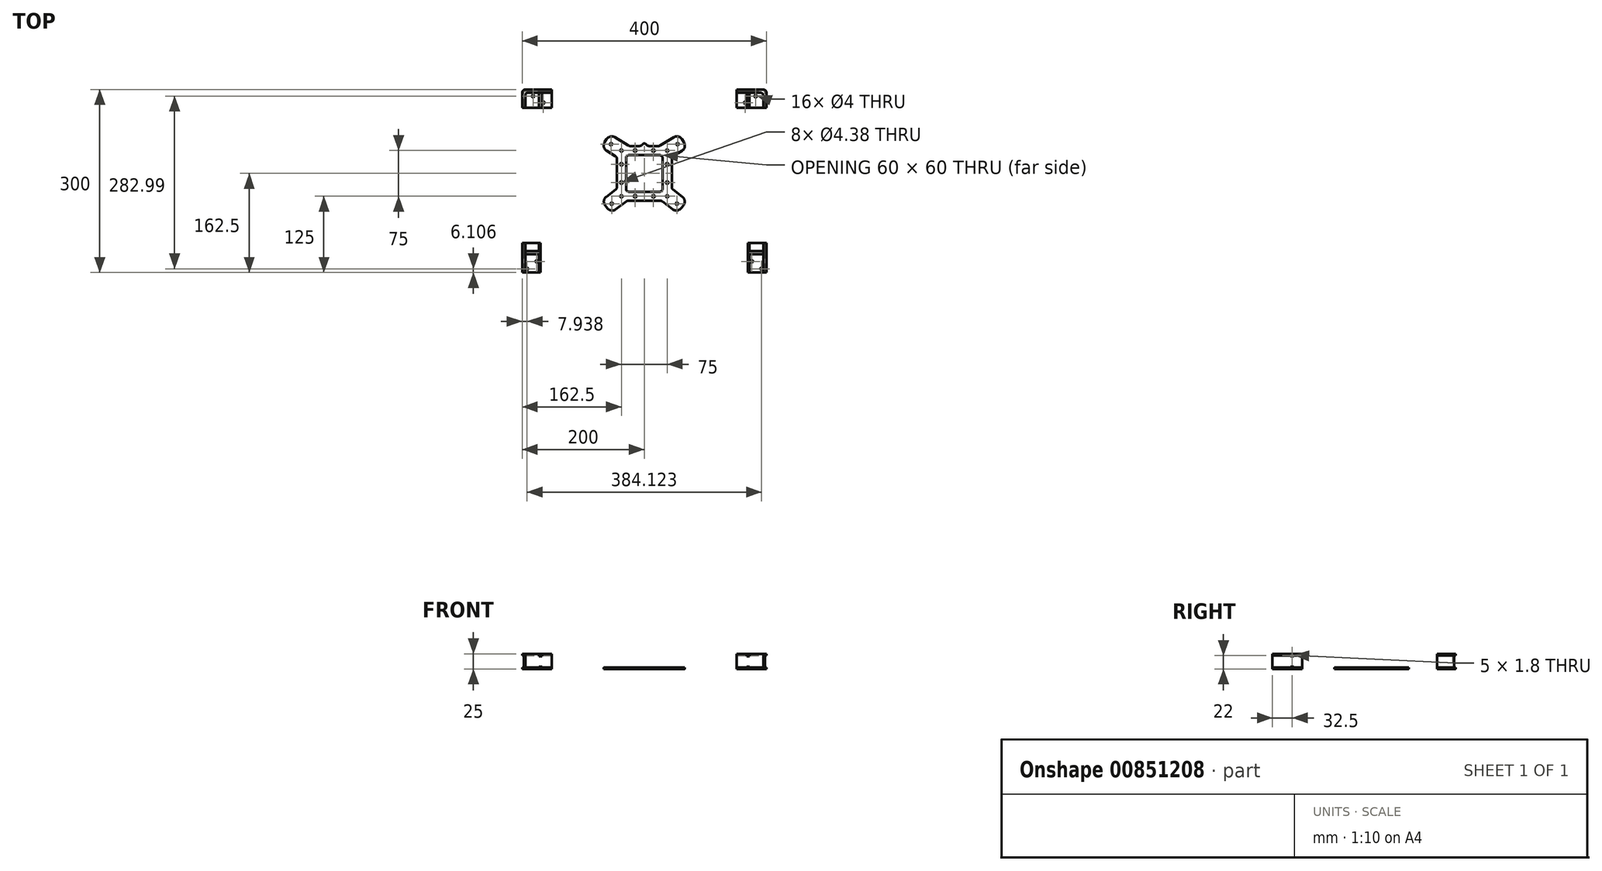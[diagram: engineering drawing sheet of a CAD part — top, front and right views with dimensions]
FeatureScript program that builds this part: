
annotation { "Feature Type Name" : "Feature", "Feature Type Description" : "" }
export const myFeature = defineFeature(function(context is Context, id is Id, definition is map)
    precondition{}
    {
        {
            assignVariable(context, id + "F0", {"name" : "Alto", "anyValue" : 25});
        }
        {
            var Q0;
            Q0=qCreatedBy(makeId("Top.planeOp"),FACE);
            var sketch = newSketch(context, id + "F1", { "sketchPlane" : qUnion([Q0])});
            skLineSegment(sketch, "E0.bottom", {"start": v(-37.5, -37.5) * mm, "end": v(37.5, -37.5) * mm, "construction": true});
            skLineSegment(sketch, "E0.top", {"start": v(-37.5, 37.5) * mm, "end": v(37.5, 37.5) * mm, "construction": true});
            skLineSegment(sketch, "E0.left", {"start": v(-37.5, -37.5) * mm, "end": v(-37.5, 37.5) * mm, "construction": true});
            skLineSegment(sketch, "E0.right", {"start": v(37.5, -37.5) * mm, "end": v(37.5, 37.5) * mm, "construction": true});
            skPoint(sketch, "E0.middle", {"position": v(0, 0) * mm});
            skCircle(sketch, "E1", {"center": v(-37.5, 37.5) * mm, "radius": 2 * mm});
            skCircle(sketch, "E2", {"center": v(37.5, 37.5) * mm, "radius": 2 * mm});
            skCircle(sketch, "E3", {"center": v(37.5, -37.5) * mm, "radius": 2 * mm});
            skCircle(sketch, "E4", {"center": v(-37.5, -37.5) * mm, "radius": 2 * mm});
            skLineSegment(sketch, "E5.bottom", {"start": v(25, -30) * mm, "end": v(-25, -30) * mm});
            skLineSegment(sketch, "E5.top", {"start": v(25, 30) * mm, "end": v(-25, 30) * mm});
            skLineSegment(sketch, "E5.left", {"start": v(30, -25) * mm, "end": v(30, 25) * mm});
            skLineSegment(sketch, "E5.right", {"start": v(-30, -25) * mm, "end": v(-30, 25) * mm});
            skLineSegment(sketch, "E6.bottom", {"start": v(-23.58, 45) * mm, "end": v(-7.48, 45) * mm});
            skLineSegment(sketch, "E6.left", {"start": v(-45, 24.13) * mm, "end": v(-45, -22.54) * mm});
            skLineSegment(sketch, "E6.right", {"start": v(45, 40) * mm, "end": v(45, -40) * mm});
            skPoint(sketch, "E7.visualSharp", {"position": v(-30, 30) * mm});
            skArc(sketch, "E7.filletArc", {"start": v(-25, 30) * mm, "mid": v(-28.54, 28.54) * mm, "end": v(-30, 25) * mm});
            skPoint(sketch, "E8.visualSharp", {"position": v(30, 30) * mm});
            skArc(sketch, "E8.filletArc", {"start": v(30, 25) * mm, "mid": v(28.54, 28.54) * mm, "end": v(25, 30) * mm});
            skPoint(sketch, "E9.visualSharp", {"position": v(30, -30) * mm});
            skArc(sketch, "E9.filletArc", {"start": v(25, -30) * mm, "mid": v(28.54, -28.54) * mm, "end": v(30, -25) * mm});
            skPoint(sketch, "E10.visualSharp", {"position": v(-30, -30) * mm});
            skArc(sketch, "E10.filletArc", {"start": v(-30, -25) * mm, "mid": v(-28.54, -28.54) * mm, "end": v(-25, -30) * mm});
            skPoint(sketch, "E11.visualSharp", {"position": v(45, 45) * mm});
            skArc(sketch, "E11.filletArc", {"start": v(45, 40) * mm, "mid": v(43.54, 43.54) * mm, "end": v(40, 45) * mm});
            skPoint(sketch, "E12.visualSharp", {"position": v(-45, 45) * mm});
            skPoint(sketch, "E13.visualSharp", {"position": v(45, -45) * mm});
            skArc(sketch, "E13.filletArc", {"start": v(40, -45) * mm, "mid": v(43.54, -43.54) * mm, "end": v(45, -40) * mm});
            skPoint(sketch, "E14.visualSharp", {"position": v(-45, -45) * mm});
            skLineSegment(sketch, "E15", {"start": v(-37.5, -37.5) * mm, "end": v(-37.5, -162.5) * mm, "construction": true});
            skLineSegment(sketch, "E16", {"start": v(0, 0) * mm, "end": v(0, -162.5) * mm, "construction": true});
            skLineSegment(sketch, "E17", {"start": v(0, -162.5) * mm, "end": v(200, -162.5) * mm});
            skLineSegment(sketch, "E18", {"start": v(200, -162.5) * mm, "end": v(200, 137.5) * mm, "construction": true});
            skLineSegment(sketch, "E19", {"start": v(200, 137.5) * mm, "end": v(-200, 137.5) * mm, "construction": true});
            skLineSegment(sketch, "E20", {"start": v(-200, 137.5) * mm, "end": v(-200, -162.5) * mm, "construction": true});
            skLineSegment(sketch, "E21", {"start": v(-200, -162.5) * mm, "end": v(0, -162.5) * mm, "construction": true});
            skLineSegment(sketch, "E22", {"start": v(-37.5, 37.5) * mm, "end": v(-200, 137.5) * mm, "construction": true});
            skLineSegment(sketch, "E23", {"start": v(-26.2, 45.74) * mm, "end": v(-56.68, 64.5) * mm});
            skLineSegment(sketch, "E24", {"start": v(-56.68, 64.5) * mm, "end": v(-63.46, 53.47) * mm});
            skLineSegment(sketch, "E25.MirrorCS", {"start": v(-47.38, 28.39) * mm, "end": v(-70.24, 42.45) * mm});
            skLineSegment(sketch, "E26.MirrorCS", {"start": v(-70.24, 42.45) * mm, "end": v(-63.46, 53.47) * mm});
            skPoint(sketch, "E27.orphan", {"position": v(-38.56, 22.96) * mm});
            skPoint(sketch, "E28.visualSharp", {"position": v(-45, 26.92) * mm});
            skArc(sketch, "E28.filletArc", {"start": v(-45, 24.13) * mm, "mid": v(-45.64, 26.57) * mm, "end": v(-47.38, 28.39) * mm});
            skPoint(sketch, "E29.visualSharp", {"position": v(-25, 45) * mm});
            skArc(sketch, "E29.filletArc", {"start": v(-26.2, 45.74) * mm, "mid": v(-24.95, 45.19) * mm, "end": v(-23.58, 45) * mm});
            skLineSegment(sketch, "E30", {"start": v(-37.5, 37.5) * mm, "end": v(-39.84, 33.7) * mm, "construction": true});
            skLineSegment(sketch, "E31", {"start": v(-39.84, 33.7) * mm, "end": v(-56.88, 44.17) * mm, "construction": true});
            skLineSegment(sketch, "E32", {"start": v(-56.88, 44.17) * mm, "end": v(-54.53, 47.98) * mm, "construction": true});
            skCircle(sketch, "E33", {"center": v(-54.53, 47.98) * mm, "radius": 2 * mm});
            skLineSegment(sketch, "E34.bottom", {"start": v(-200, 137.5) * mm, "end": v(-151.5, 137.5) * mm});
            skLineSegment(sketch, "E34.top", {"start": v(-200, 107.5) * mm, "end": v(-151.5, 107.5) * mm});
            skLineSegment(sketch, "E34.left", {"start": v(-200, 137.5) * mm, "end": v(-200, 107.5) * mm});
            skLineSegment(sketch, "E34.right", {"start": v(-151.5, 137.5) * mm, "end": v(-151.5, 107.5) * mm});
            skLineSegment(sketch, "E35.bottom", {"start": v(-151.5, 107.5) * mm, "end": v(-195, 107.5) * mm});
            skLineSegment(sketch, "E35.top", {"start": v(-151.5, 132.5) * mm, "end": v(-195, 132.5) * mm});
            skLineSegment(sketch, "E35.left", {"start": v(-151.5, 107.5) * mm, "end": v(-151.5, 132.5) * mm});
            skLineSegment(sketch, "E35.right", {"start": v(-195, 107.5) * mm, "end": v(-195, 132.5) * mm});
            skLineSegment(sketch, "E36", {"start": v(-56.88, 44.17) * mm, "end": v(-167.6, 112.3) * mm, "construction": true});
            skLineSegment(sketch, "E37", {"start": v(-167.6, 112.3) * mm, "end": v(-165.25, 116.11) * mm, "construction": true});
            skCircle(sketch, "E38", {"center": v(-165.25, 116.11) * mm, "radius": 2 * mm});
            skLineSegment(sketch, "E39", {"start": v(-167.6, 112.3) * mm, "end": v(-184.63, 122.79) * mm, "construction": true});
            skLineSegment(sketch, "E40", {"start": v(-184.63, 122.79) * mm, "end": v(-182.28, 126.6) * mm, "construction": true});
            skCircle(sketch, "E41", {"center": v(-182.28, 126.6) * mm, "radius": 2 * mm});
            skLineSegment(sketch, "E42", {"start": v(0, -34.68) * mm, "end": v(15, -34.68) * mm, "construction": true});
            skCircle(sketch, "E43", {"center": v(15, -37.5) * mm, "radius": 2.2 * mm});
            skLineSegment(sketch, "E44", {"start": v(0, 0) * mm, "end": v(-16.78, 0) * mm, "construction": true});
            skLineSegment(sketch, "E45", {"start": v(0, 0) * mm, "end": v(-10.77, -10.77) * mm, "construction": true});
            skCircle(sketch, "E46.MirrorC", {"center": v(-15, -37.5) * mm, "radius": 2.2 * mm});
            skCircle(sketch, "E47.MirrorC", {"center": v(-37.5, 15) * mm, "radius": 2.2 * mm});
            skCircle(sketch, "E48.MirrorC", {"center": v(-37.5, -15) * mm, "radius": 2.2 * mm});
            skCircle(sketch, "E49.MirrorC", {"center": v(-15, 37.5) * mm, "radius": 2.2 * mm});
            skCircle(sketch, "E50.MirrorC", {"center": v(15, 37.5) * mm, "radius": 2.2 * mm});
            skCircle(sketch, "E51.MirrorC", {"center": v(37.5, -15) * mm, "radius": 2.2 * mm});
            skCircle(sketch, "E52.MirrorC", {"center": v(37.5, 15) * mm, "radius": 2.2 * mm});
            skLineSegment(sketch, "E53", {"start": v(0, 0) * mm, "end": v(-200, 0) * mm, "construction": true});
            skLineSegment(sketch, "E54", {"start": v(0, 0) * mm, "end": v(0, 137.5) * mm, "construction": true});
            skLineSegment(sketch, "E55.MirrorCS", {"start": v(167.6, 112.3) * mm, "end": v(165.25, 116.11) * mm, "construction": true});
            skCircle(sketch, "E56.MirrorC", {"center": v(165.25, 116.11) * mm, "radius": 2 * mm});
            skCircle(sketch, "E57.MirrorC", {"center": v(182.28, 126.6) * mm, "radius": 2 * mm});
            skLineSegment(sketch, "E58.MirrorCS", {"start": v(184.63, 122.79) * mm, "end": v(182.28, 126.6) * mm, "construction": true});
            skLineSegment(sketch, "E59.MirrorCS", {"start": v(151.5, 107.5) * mm, "end": v(151.5, 132.5) * mm});
            skLineSegment(sketch, "E60.MirrorCS", {"start": v(151.5, 107.5) * mm, "end": v(195, 107.5) * mm});
            skLineSegment(sketch, "E61.MirrorCS", {"start": v(151.5, 132.5) * mm, "end": v(195, 132.5) * mm});
            skLineSegment(sketch, "E62.MirrorCS", {"start": v(200, 137.5) * mm, "end": v(151.5, 137.5) * mm});
            skLineSegment(sketch, "E63.MirrorCS", {"start": v(151.5, 137.5) * mm, "end": v(151.5, 107.5) * mm});
            skLineSegment(sketch, "E64.MirrorCS", {"start": v(195, 107.5) * mm, "end": v(195, 132.5) * mm});
            skLineSegment(sketch, "E65.MirrorCS", {"start": v(167.6, 112.3) * mm, "end": v(184.63, 122.79) * mm, "construction": true});
            skLineSegment(sketch, "E66.MirrorCS", {"start": v(200, 107.5) * mm, "end": v(151.5, 107.5) * mm});
            skLineSegment(sketch, "E67.MirrorCS", {"start": v(200, 137.5) * mm, "end": v(200, 107.5) * mm});
            skLineSegment(sketch, "E68", {"start": v(-37.5, -37.5) * mm, "end": v(-200, -162.5) * mm, "construction": true});
            skLineSegment(sketch, "E69.bottom", {"start": v(-200, -162.5) * mm, "end": v(-170, -162.5) * mm});
            skLineSegment(sketch, "E69.top", {"start": v(-200, -114) * mm, "end": v(-170, -114) * mm});
            skLineSegment(sketch, "E69.left", {"start": v(-200, -162.5) * mm, "end": v(-200, -114) * mm});
            skLineSegment(sketch, "E69.right", {"start": v(-170, -162.5) * mm, "end": v(-170, -114) * mm});
            skLineSegment(sketch, "E70", {"start": v(-46.95, -26.5) * mm, "end": v(-70.24, -44.42) * mm});
            skLineSegment(sketch, "E71", {"start": v(-70.24, 42.45) * mm, "end": v(-70.24, -45.57) * mm, "construction": true});
            skLineSegment(sketch, "E72", {"start": v(-70.24, -44.42) * mm, "end": v(-54.47, -64.92) * mm});
            skLineSegment(sketch, "E73", {"start": v(-54.47, -64.92) * mm, "end": v(-29.92, -46.04) * mm});
            skLineSegment(sketch, "E74", {"start": v(-37.5, -37.5) * mm, "end": v(-40.46, -33.65) * mm, "construction": true});
            skLineSegment(sketch, "E75", {"start": v(-40.46, -33.65) * mm, "end": v(-56.31, -45.85) * mm, "construction": true});
            skLineSegment(sketch, "E76", {"start": v(-56.31, -45.85) * mm, "end": v(-53.35, -49.7) * mm, "construction": true});
            skCircle(sketch, "E77", {"center": v(-53.35, -49.7) * mm, "radius": 2 * mm});
            skLineSegment(sketch, "E78", {"start": v(-56.31, -45.85) * mm, "end": v(-179.17, -140.35) * mm, "construction": true});
            skLineSegment(sketch, "E79", {"start": v(-179.17, -140.35) * mm, "end": v(-176.2, -144.2) * mm, "construction": true});
            skCircle(sketch, "E80", {"center": v(-176.2, -144.2) * mm, "radius": 2 * mm});
            skLineSegment(sketch, "E81", {"start": v(-179.17, -140.35) * mm, "end": v(-195.02, -152.55) * mm, "construction": true});
            skLineSegment(sketch, "E82", {"start": v(-195.02, -152.55) * mm, "end": v(-192.06, -156.4) * mm, "construction": true});
            skCircle(sketch, "E83", {"center": v(-192.06, -156.4) * mm, "radius": 2 * mm});
            skLineSegment(sketch, "E84.bottom", {"start": v(-170, -114) * mm, "end": v(-195, -114) * mm});
            skLineSegment(sketch, "E84.top", {"start": v(-170, -162.5) * mm, "end": v(-195, -162.5) * mm});
            skLineSegment(sketch, "E84.left", {"start": v(-170, -114) * mm, "end": v(-170, -162.5) * mm});
            skLineSegment(sketch, "E84.right", {"start": v(-195, -114) * mm, "end": v(-195, -162.5) * mm});
            skLineSegment(sketch, "E85.MirrorCS", {"start": v(179.17, -140.35) * mm, "end": v(176.2, -144.2) * mm, "construction": true});
            skCircle(sketch, "E86.MirrorC", {"center": v(176.2, -144.2) * mm, "radius": 2 * mm});
            skCircle(sketch, "E87.MirrorC", {"center": v(192.06, -156.4) * mm, "radius": 2 * mm});
            skLineSegment(sketch, "E88.MirrorCS", {"start": v(195.02, -152.55) * mm, "end": v(192.06, -156.4) * mm, "construction": true});
            skLineSegment(sketch, "E89.MirrorCS", {"start": v(170, -162.5) * mm, "end": v(170, -114) * mm});
            skLineSegment(sketch, "E90.MirrorCS", {"start": v(179.17, -140.35) * mm, "end": v(195.02, -152.55) * mm, "construction": true});
            skLineSegment(sketch, "E91.MirrorCS", {"start": v(170, -162.5) * mm, "end": v(195, -162.5) * mm});
            skLineSegment(sketch, "E92.MirrorCS", {"start": v(200, -114) * mm, "end": v(170, -114) * mm});
            skLineSegment(sketch, "E93.MirrorCS", {"start": v(170, -114) * mm, "end": v(195, -114) * mm});
            skLineSegment(sketch, "E94.MirrorCS", {"start": v(200, -162.5) * mm, "end": v(200, -114) * mm});
            skLineSegment(sketch, "E95.MirrorCS", {"start": v(170, -114) * mm, "end": v(170, -162.5) * mm});
            skLineSegment(sketch, "E96.MirrorCS", {"start": v(200, -162.5) * mm, "end": v(170, -162.5) * mm});
            skLineSegment(sketch, "E97.MirrorCS", {"start": v(195, -114) * mm, "end": v(195, -162.5) * mm});
            skLineSegment(sketch, "E98.trimOffspring", {"start": v(-26.87, -45) * mm, "end": v(40, -45) * mm});
            skPoint(sketch, "E99.visualSharp", {"position": v(-45, -25) * mm});
            skArc(sketch, "E99.filletArc", {"start": v(-46.95, -26.5) * mm, "mid": v(-45.51, -24.75) * mm, "end": v(-45, -22.54) * mm});
            skPoint(sketch, "E100.visualSharp", {"position": v(-28.57, -45) * mm});
            skArc(sketch, "E100.filletArc", {"start": v(-26.87, -45) * mm, "mid": v(-28.48, -45.27) * mm, "end": v(-29.92, -46.04) * mm});
            skPoint(sketch, "E101.MirrorP", {"position": v(28.57, -45) * mm});
            skArc(sketch, "E102.MirrorCS", {"start": v(26.87, -45) * mm, "mid": v(28.48, -45.27) * mm, "end": v(29.92, -46.04) * mm});
            skLineSegment(sketch, "E103.MirrorCS", {"start": v(54.47, -64.92) * mm, "end": v(29.92, -46.04) * mm});
            skArc(sketch, "E104.MirrorCS", {"start": v(46.95, -26.5) * mm, "mid": v(45.51, -24.75) * mm, "end": v(45, -22.54) * mm});
            skLineSegment(sketch, "E105.MirrorCS", {"start": v(46.95, -26.5) * mm, "end": v(70.24, -44.42) * mm});
            skCircle(sketch, "E106.MirrorC", {"center": v(53.35, -49.7) * mm, "radius": 2 * mm});
            skLineSegment(sketch, "E107.MirrorCS", {"start": v(70.24, -44.42) * mm, "end": v(54.47, -64.92) * mm});
            skArc(sketch, "E108.MirrorCS", {"start": v(26.2, 45.74) * mm, "mid": v(24.95, 45.19) * mm, "end": v(23.58, 45) * mm});
            skLineSegment(sketch, "E109.MirrorCS", {"start": v(26.2, 45.74) * mm, "end": v(56.68, 64.5) * mm});
            skArc(sketch, "E110.MirrorCS", {"start": v(45, 24.13) * mm, "mid": v(45.64, 26.57) * mm, "end": v(47.38, 28.39) * mm});
            skLineSegment(sketch, "E111.MirrorCS", {"start": v(47.38, 28.39) * mm, "end": v(70.24, 42.45) * mm});
            skLineSegment(sketch, "E112.MirrorCS", {"start": v(56.68, 64.5) * mm, "end": v(63.46, 53.47) * mm});
            skCircle(sketch, "E113.MirrorC", {"center": v(54.53, 47.98) * mm, "radius": 2 * mm});
            skLineSegment(sketch, "E114.MirrorCS", {"start": v(70.24, 42.45) * mm, "end": v(63.46, 53.47) * mm});
            skArc(sketch, "E115", {"start": v(3.33, 47.22) * mm, "mid": v(0, 49) * mm, "end": v(-3.33, 47.22) * mm});
            skLineSegment(sketch, "E116.trimOffspring", {"start": v(7.48, 45) * mm, "end": v(40, 45) * mm});
            skPoint(sketch, "E117.visualSharp", {"position": v(4, 45) * mm});
            skArc(sketch, "E117.filletArc", {"start": v(3.33, 47.22) * mm, "mid": v(5.13, 45.6) * mm, "end": v(7.48, 45) * mm});
            skPoint(sketch, "E118.visualSharp", {"position": v(-4, 45) * mm});
            skArc(sketch, "E118.filletArc", {"start": v(-7.48, 45) * mm, "mid": v(-5.13, 45.6) * mm, "end": v(-3.33, 47.22) * mm});
            skLineSegment(sketch, "E119", {"start": v(-165.25, 116.11) * mm, "end": v(-161.58, 122.08) * mm, "construction": true});
            skLineSegment(sketch, "E120", {"start": v(-161.58, 122.08) * mm, "end": v(-151.5, 115.87) * mm});
            skLineSegment(sketch, "E121", {"start": v(-161.58, 122.08) * mm, "end": v(-178.52, 132.5) * mm});
            skLineSegment(sketch, "E122.MirrorCS", {"start": v(-30.16, 49.42) * mm, "end": v(-192.66, 149.42) * mm, "construction": true});
            skLineSegment(sketch, "E123.MirrorCS", {"start": v(-168.92, 110.15) * mm, "end": v(-185.86, 120.58) * mm});
            skLineSegment(sketch, "E124", {"start": v(-168.92, 110.15) * mm, "end": v(-164.6, 107.5) * mm});
            skLineSegment(sketch, "E125", {"start": v(-185.86, 120.58) * mm, "end": v(-195, 126.2) * mm});
            skLineSegment(sketch, "E126", {"start": v(-164.6, 107.5) * mm, "end": v(-157.27, 119.42) * mm});
            skSolve(sketch);
        }
        {
            var Q0;
            Q0 = qSketchRegion(id + "F1", true);
            extrude(context, id + "F2", {"entities" : qUnion([Q0]), "depth" : 2.5 * mm, "offsetDistance" : 25 * mm});
        }
        {
            var Q0;
            Q0=makeQuery(id+"F1.imprint","IMPRINT",FACE,{"disambiguationData":[TD([[makeQuery(id+"F1.imprint","IMPRINT",EDGE,{"derivedFrom":sQuery(id+"F1.wireOp",EDGE,"E34.bottom")}),-1.0]])]});
            var Q1;
            Q1=makeQuery(id+"F1.imprint","IMPRINT",FACE,{"disambiguationData":[TD([[makeQuery(id+"F1.imprint","IMPRINT",EDGE,{"derivedFrom":sQuery(id+"F1.wireOp",EDGE,"E69.bottom")}),1.0]])]});
            var Q2;
            Q2=makeQuery(id+"F1.imprint","IMPRINT",FACE,{"disambiguationData":[TD([[makeQuery(id+"F1.imprint","IMPRINT",EDGE,{"derivedFrom":sQuery(id+"F1.wireOp",EDGE,"E92.MirrorCS")}),1.0]])]});
            var Q3;
            {var subQ2=sQuery(id+"F1.wireOp",EDGE,"E61.MirrorCS");Q3=makeQuery(id+"F1.imprint","IMPRINT",FACE,{"disambiguationData":[TD([[makeQuery(id+"F1.imprint","IMPRINT",EDGE,{"derivedFrom":subQ2}),1.0]])]});}
            extrude(context, id + "F3", {"entities" : qUnion([Q0, Q1, Q2, Q3]), "operationType" : NewBodyOperationType.ADD, "depth" : (getVariable(context, 'Alto')) * mm, "offsetDistance" : 25 * mm});
        }
        {
            var Q0;
            Q0=qCreatedBy(makeId("Right.planeOp"),FACE);
            var sketch = newSketch(context, id + "F4", { "sketchPlane" : qUnion([Q0])});
            skLineSegment(sketch, "E127", {"start": v(0, 0) * mm, "end": v(137.5, 0) * mm, "construction": true});
            skLineSegment(sketch, "E128", {"start": v(137.5, 0) * mm, "end": v(137.5, 2.5) * mm, "construction": true});
            skLineSegment(sketch, "E129", {"start": v(137.5, 2.5) * mm, "end": v(135, 2.5) * mm});
            skLineSegment(sketch, "E130", {"start": v(135, 2.5) * mm, "end": v(135, 22.5) * mm});
            skLineSegment(sketch, "E131", {"start": v(135, 22.5) * mm, "end": v(137.5, 22.5) * mm});
            skLineSegment(sketch, "E132", {"start": v(137.5, 22.5) * mm, "end": v(137.5, 2.5) * mm});
            skLineSegment(sketch, "E133", {"start": v(0, 0) * mm, "end": v(-130, 0) * mm, "construction": true});
            skLineSegment(sketch, "E134", {"start": v(-130, 0) * mm, "end": v(-130, 3) * mm, "construction": true});
            skLineSegment(sketch, "E135.bottom", {"start": v(-132.5, 2.1) * mm, "end": v(-127.5, 2.1) * mm});
            skLineSegment(sketch, "E135.top", {"start": v(-132.5, 3.9) * mm, "end": v(-127.5, 3.9) * mm});
            skLineSegment(sketch, "E135.left", {"start": v(-132.5, 2.1) * mm, "end": v(-132.5, 3.9) * mm});
            skLineSegment(sketch, "E135.right", {"start": v(-127.5, 2.1) * mm, "end": v(-127.5, 3.9) * mm});
            skPoint(sketch, "E135.middle", {"position": v(-130, 3) * mm});
            skLineSegment(sketch, "E136", {"start": v(-130, 3) * mm, "end": v(-130, 12.5) * mm, "construction": true});
            skLineSegment(sketch, "E137", {"start": v(-145.6, 12.5) * mm, "end": v(-130, 12.5) * mm, "construction": true});
            skLineSegment(sketch, "E138.MirrorCS", {"start": v(-132.5, 21.1) * mm, "end": v(-127.5, 21.1) * mm});
            skLineSegment(sketch, "E139.MirrorCS", {"start": v(-132.5, 22.9) * mm, "end": v(-127.5, 22.9) * mm});
            skLineSegment(sketch, "E140.MirrorCS", {"start": v(-127.5, 22.9) * mm, "end": v(-127.5, 21.1) * mm});
            skPoint(sketch, "E141.MirrorP", {"position": v(-130, 22) * mm});
            skLineSegment(sketch, "E142.MirrorCS", {"start": v(-132.5, 22.9) * mm, "end": v(-132.5, 21.1) * mm});
            skSolve(sketch);
        }
        {
            var Q0;
            Q0 = qSketchRegion(id + "F4", true);
            extrude(context, id + "F5", {"entities" : qUnion([Q0]), "operationType" : NewBodyOperationType.REMOVE, "endBound" : BoundingType.THROUGH_ALL, "oppositeDirection" : true, "depth" : 25 * mm, "offsetDistance" : 25 * mm, "hasSecondDirection" : true, "secondDirectionBound" : SecondDirectionBoundingType.THROUGH_ALL, "secondDirectionOppositeDirection" : false, "secondDirectionDepth" : 25 * mm});
        }
        {
            var Q0;
            Q0=qCreatedBy(makeId("Front.planeOp"),FACE);
            var sketch = newSketch(context, id + "F6", { "sketchPlane" : qUnion([Q0])});
            skLineSegment(sketch, "E143", {"start": v(0, 0) * mm, "end": v(200, 0) * mm, "construction": true});
            skLineSegment(sketch, "E144", {"start": v(200, 0) * mm, "end": v(200, 2.5) * mm, "construction": true});
            skLineSegment(sketch, "E145.bottom", {"start": v(200, 2.5) * mm, "end": v(197.5, 2.5) * mm});
            skLineSegment(sketch, "E145.top", {"start": v(200, 22.5) * mm, "end": v(197.5, 22.5) * mm});
            skLineSegment(sketch, "E145.left", {"start": v(200, 2.5) * mm, "end": v(200, 22.5) * mm});
            skLineSegment(sketch, "E145.right", {"start": v(197.5, 2.5) * mm, "end": v(197.5, 22.5) * mm});
            skLineSegment(sketch, "E146", {"start": v(0, 0) * mm, "end": v(0, 29.34) * mm, "construction": true});
            skLineSegment(sketch, "E147.MirrorCS", {"start": v(-200, 22.5) * mm, "end": v(-197.5, 22.5) * mm});
            skLineSegment(sketch, "E148.MirrorCS", {"start": v(-200, 0) * mm, "end": v(-200, 2.5) * mm, "construction": true});
            skLineSegment(sketch, "E149.MirrorCS", {"start": v(-200, 2.5) * mm, "end": v(-197.5, 2.5) * mm});
            skLineSegment(sketch, "E150.MirrorCS", {"start": v(-200, 2.5) * mm, "end": v(-200, 22.5) * mm});
            skLineSegment(sketch, "E151.MirrorCS", {"start": v(-197.5, 2.5) * mm, "end": v(-197.5, 22.5) * mm});
            skLineSegment(sketch, "E152", {"start": v(0, 0) * mm, "end": v(-170, 0) * mm, "construction": true});
            skLineSegment(sketch, "E153", {"start": v(-170, 0) * mm, "end": v(-170, 3) * mm, "construction": true});
            skLineSegment(sketch, "E154.bottom", {"start": v(-167.5, 3.9) * mm, "end": v(-172.5, 3.9) * mm});
            skLineSegment(sketch, "E154.top", {"start": v(-167.5, 2.1) * mm, "end": v(-172.5, 2.1) * mm});
            skLineSegment(sketch, "E154.left", {"start": v(-167.5, 3.9) * mm, "end": v(-167.5, 2.1) * mm});
            skLineSegment(sketch, "E154.right", {"start": v(-172.5, 3.9) * mm, "end": v(-172.5, 2.1) * mm});
            skPoint(sketch, "E154.middle", {"position": v(-170, 3) * mm});
            skLineSegment(sketch, "E155", {"start": v(-170, 3) * mm, "end": v(-170, 12.5) * mm, "construction": true});
            skLineSegment(sketch, "E156", {"start": v(-170, 12.5) * mm, "end": v(-173.36, 12.5) * mm, "construction": true});
            skPoint(sketch, "E157.MirrorP", {"position": v(-170, 22) * mm});
            skLineSegment(sketch, "E158.MirrorCS", {"start": v(-167.5, 22.9) * mm, "end": v(-172.5, 22.9) * mm});
            skLineSegment(sketch, "E159.MirrorCS", {"start": v(-172.5, 21.1) * mm, "end": v(-172.5, 22.9) * mm});
            skLineSegment(sketch, "E160.MirrorCS", {"start": v(-167.5, 21.1) * mm, "end": v(-167.5, 22.9) * mm});
            skLineSegment(sketch, "E161.MirrorCS", {"start": v(-167.5, 21.1) * mm, "end": v(-172.5, 21.1) * mm});
            skLineSegment(sketch, "E162.MirrorCS", {"start": v(167.5, 3.9) * mm, "end": v(167.5, 2.1) * mm});
            skLineSegment(sketch, "E163.MirrorCS", {"start": v(167.5, 2.1) * mm, "end": v(172.5, 2.1) * mm});
            skLineSegment(sketch, "E164.MirrorCS", {"start": v(172.5, 3.9) * mm, "end": v(172.5, 2.1) * mm});
            skLineSegment(sketch, "E165.MirrorCS", {"start": v(167.5, 21.1) * mm, "end": v(167.5, 22.9) * mm});
            skLineSegment(sketch, "E166.MirrorCS", {"start": v(167.5, 3.9) * mm, "end": v(172.5, 3.9) * mm});
            skLineSegment(sketch, "E167.MirrorCS", {"start": v(172.5, 21.1) * mm, "end": v(172.5, 22.9) * mm});
            skLineSegment(sketch, "E168.MirrorCS", {"start": v(170, 0) * mm, "end": v(170, 3) * mm, "construction": true});
            skLineSegment(sketch, "E169.MirrorCS", {"start": v(167.5, 22.9) * mm, "end": v(172.5, 22.9) * mm});
            skLineSegment(sketch, "E170.MirrorCS", {"start": v(170, 12.5) * mm, "end": v(173.36, 12.5) * mm, "construction": true});
            skLineSegment(sketch, "E171.MirrorCS", {"start": v(167.5, 21.1) * mm, "end": v(172.5, 21.1) * mm});
            skLineSegment(sketch, "E172.MirrorCS", {"start": v(170, 3) * mm, "end": v(170, 12.5) * mm, "construction": true});
            skPoint(sketch, "E173.MirrorP", {"position": v(170, 22) * mm});
            skPoint(sketch, "E174.MirrorP", {"position": v(170, 3) * mm});
            skSolve(sketch);
        }
        {
            var Q0;
            Q0 = qSketchRegion(id + "F6", true);
            extrude(context, id + "F7", {"entities" : qUnion([Q0]), "operationType" : NewBodyOperationType.REMOVE, "endBound" : BoundingType.THROUGH_ALL, "depth" : 25 * mm, "offsetDistance" : 25 * mm, "hasSecondDirection" : true, "secondDirectionBound" : SecondDirectionBoundingType.THROUGH_ALL, "secondDirectionOppositeDirection" : true, "secondDirectionDepth" : 25 * mm});
        }
        {
            var Q0;
            Q0=makeQuery(id+"F2.opExtrude","SWEPT_EDGE",EDGE,{"disambiguationData":[OSD([sQuery(id+"F1.wireOp",EDGE,"E35.bottom"),sQuery(id+"F1.wireOp",EDGE,"E35.left")])]});
            var Q1;
            Q1=makeQuery(id+"F2.opExtrude","SWEPT_EDGE",EDGE,{"disambiguationData":[OSD([sQuery(id+"F1.wireOp",EDGE,"E25.MirrorCS"),sQuery(id+"F1.wireOp",EDGE,"E26.MirrorCS")])]});
            var Q2;
            Q2=makeQuery(id+"F2.opExtrude","SWEPT_EDGE",EDGE,{"disambiguationData":[OSD([sQuery(id+"F1.wireOp",EDGE,"E23"),sQuery(id+"F1.wireOp",EDGE,"E24")])]});
            var Q3;
            Q3=makeQuery(id+"F2.opExtrude","SWEPT_EDGE",EDGE,{"disambiguationData":[OSD([sQuery(id+"F1.wireOp",EDGE,"E63.MirrorCS"),sQuery(id+"F1.wireOp",EDGE,"E66.MirrorCS")])]});
            var Q4;
            Q4=makeQuery(id+"F2.opExtrude","SWEPT_EDGE",EDGE,{"disambiguationData":[OSD([sQuery(id+"F1.wireOp",EDGE,"E109.MirrorCS"),sQuery(id+"F1.wireOp",EDGE,"E112.MirrorCS")])]});
            var Q5;
            Q5=makeQuery(id+"F2.opExtrude","SWEPT_EDGE",EDGE,{"disambiguationData":[OSD([sQuery(id+"F1.wireOp",EDGE,"E111.MirrorCS"),sQuery(id+"F1.wireOp",EDGE,"E114.MirrorCS")])]});
            var Q6;
            Q6=makeQuery(id+"F2.opExtrude","SWEPT_EDGE",EDGE,{"disambiguationData":[OSD([sQuery(id+"F1.wireOp",EDGE,"E105.MirrorCS"),sQuery(id+"F1.wireOp",EDGE,"E107.MirrorCS")])]});
            var Q7;
            Q7=makeQuery(id+"F2.opExtrude","SWEPT_EDGE",EDGE,{"disambiguationData":[OSD([sQuery(id+"F1.wireOp",EDGE,"E103.MirrorCS"),sQuery(id+"F1.wireOp",EDGE,"E107.MirrorCS")])]});
            var Q8;
            Q8=makeQuery(id+"F2.opExtrude","SWEPT_EDGE",EDGE,{"disambiguationData":[OSD([sQuery(id+"F1.wireOp",EDGE,"E72"),sQuery(id+"F1.wireOp",EDGE,"E73")])]});
            var Q9;
            Q9=makeQuery(id+"F2.opExtrude","SWEPT_EDGE",EDGE,{"disambiguationData":[OSD([sQuery(id+"F1.wireOp",EDGE,"E70"),sQuery(id+"F1.wireOp",EDGE,"E72")])]});
            var Q10;
            Q10=makeQuery(id+"F2.opExtrude","SWEPT_EDGE",EDGE,{"disambiguationData":[OSD([sQuery(id+"F1.wireOp",EDGE,"E95.MirrorCS"),sQuery(id+"F1.wireOp",EDGE,"E96.MirrorCS")])]});
            var Q11;
            Q11=makeQuery(id+"F2.opExtrude","SWEPT_EDGE",EDGE,{"disambiguationData":[OSD([sQuery(id+"F1.wireOp",EDGE,"E93.MirrorCS"),sQuery(id+"F1.wireOp",EDGE,"E95.MirrorCS")])]});
            var Q12;
            Q12=makeQuery(id+"F2.opExtrude","SWEPT_EDGE",EDGE,{"disambiguationData":[OSD([sQuery(id+"F1.wireOp",EDGE,"E84.top"),sQuery(id+"F1.wireOp",EDGE,"E84.left")])]});
            var Q13;
            Q13=makeQuery(id+"F2.opExtrude","SWEPT_EDGE",EDGE,{"disambiguationData":[OSD([sQuery(id+"F1.wireOp",EDGE,"E84.bottom"),sQuery(id+"F1.wireOp",EDGE,"E84.left")])]});
            fillet(context, id + "F8", {"entities" : qUnion([Q0, Q1, Q2, Q3, Q4, Q5, Q6, Q7, Q8, Q9, Q10, Q11, Q12, Q13]), "radius" : 10 * mm, "tangentPropagation" : true, "allowEdgeOverflow" : false});
        }
        {
            var Q0;
            {var subQ1=sQuery(id+"F1.wireOp",EDGE,"E34.left");Q0=makeQuery(id+"F7.boolean.opBoolean","INTERSECT",EDGE,{"derivedFrom":[makeQuery(id+"F5.boolean.opBoolean","SPLIT",FACE,{"disambiguationData":[TD([makeQuery(id+"F2.opExtrude","SWEPT_FACE",FACE,{"disambiguationData":[OSD([subQ1])]})])],"derivedFrom":makeQuery(id+"F5.opExtrude","SWEPT_FACE",FACE,{"disambiguationData":[OSD([sQuery(id+"F4.wireOp",EDGE,"E130")])]})}),makeQuery(id+"F7.opExtrude","SWEPT_FACE",FACE,{"disambiguationData":[OSD([sQuery(id+"F6.wireOp",EDGE,"E151.MirrorCS")])]})]});}
            var Q1;
            Q1=makeQuery(id+"F3.opExtrude","SWEPT_EDGE",EDGE,{"disambiguationData":[OSD([sQuery(id+"F1.wireOp",EDGE,"E35.top"),sQuery(id+"F1.wireOp",EDGE,"E35.right")])]});
            var Q2;
            {var subQ0=sQuery(id+"F1.wireOp",EDGE,"E34.bottom");var subQ1=sQuery(id+"F1.wireOp",EDGE,"E34.left");Q2=makeQuery(id+"F5.boolean.opBoolean","SPLIT",EDGE,{"disambiguationData":[TD([makeQuery(id+"F5.opExtrude","SWEPT_FACE",FACE,{"disambiguationData":[OSD([sQuery(id+"F4.wireOp",EDGE,"E131")])]})])],"derivedFrom":makeQuery(id+"F3.boolean.opBoolean","MERGE",EDGE,{"derivedFrom":[makeQuery(id+"F2.opExtrude","SWEPT_EDGE",EDGE,{"disambiguationData":[OSD([subQ0,subQ1])]}),makeQuery(id+"F3.opExtrude","SWEPT_EDGE",EDGE,{"disambiguationData":[OSD([subQ0,subQ1])]})]})});}
            var Q3;
            {var subQ0=sQuery(id+"F1.wireOp",EDGE,"E34.bottom");var subQ1=sQuery(id+"F1.wireOp",EDGE,"E34.left");Q3=makeQuery(id+"F5.boolean.opBoolean","SPLIT",EDGE,{"disambiguationData":[TD([makeQuery(id+"F5.opExtrude","SWEPT_FACE",FACE,{"disambiguationData":[OSD([sQuery(id+"F4.wireOp",EDGE,"E129")])]})])],"derivedFrom":makeQuery(id+"F3.boolean.opBoolean","MERGE",EDGE,{"derivedFrom":[makeQuery(id+"F2.opExtrude","SWEPT_EDGE",EDGE,{"disambiguationData":[OSD([subQ0,subQ1])]}),makeQuery(id+"F3.opExtrude","SWEPT_EDGE",EDGE,{"disambiguationData":[OSD([subQ0,subQ1])]})]})});}
            var Q4;
            {var subQ0=sQuery(id+"F1.wireOp",EDGE,"E62.MirrorCS");var subQ1=sQuery(id+"F1.wireOp",EDGE,"E67.MirrorCS");Q4=makeQuery(id+"F5.boolean.opBoolean","SPLIT",EDGE,{"disambiguationData":[TD([makeQuery(id+"F5.opExtrude","SWEPT_FACE",FACE,{"disambiguationData":[OSD([sQuery(id+"F4.wireOp",EDGE,"E131")])]})])],"derivedFrom":makeQuery(id+"F3.boolean.opBoolean","MERGE",EDGE,{"derivedFrom":[makeQuery(id+"F2.opExtrude","SWEPT_EDGE",EDGE,{"disambiguationData":[OSD([subQ0,subQ1])]}),makeQuery(id+"F3.opExtrude","SWEPT_EDGE",EDGE,{"disambiguationData":[OSD([subQ0,subQ1])]})]})});}
            var Q5;
            {var subQ0=sQuery(id+"F1.wireOp",EDGE,"E63.MirrorCS");Q5=makeQuery(id+"F7.boolean.opBoolean","INTERSECT",EDGE,{"derivedFrom":[makeQuery(id+"F5.boolean.opBoolean","SPLIT",FACE,{"disambiguationData":[TD([makeQuery(id+"F2.opExtrude","SWEPT_FACE",FACE,{"disambiguationData":[OSD([subQ0])]})])],"derivedFrom":makeQuery(id+"F5.opExtrude","SWEPT_FACE",FACE,{"disambiguationData":[OSD([sQuery(id+"F4.wireOp",EDGE,"E130")])]})}),makeQuery(id+"F7.opExtrude","SWEPT_FACE",FACE,{"disambiguationData":[OSD([sQuery(id+"F6.wireOp",EDGE,"E145.right")])]})]});}
            var Q6;
            {var subQ0=sQuery(id+"F1.wireOp",EDGE,"E62.MirrorCS");var subQ1=sQuery(id+"F1.wireOp",EDGE,"E67.MirrorCS");Q6=makeQuery(id+"F5.boolean.opBoolean","SPLIT",EDGE,{"disambiguationData":[TD([makeQuery(id+"F5.opExtrude","SWEPT_FACE",FACE,{"disambiguationData":[OSD([sQuery(id+"F4.wireOp",EDGE,"E129")])]})])],"derivedFrom":makeQuery(id+"F3.boolean.opBoolean","MERGE",EDGE,{"derivedFrom":[makeQuery(id+"F2.opExtrude","SWEPT_EDGE",EDGE,{"disambiguationData":[OSD([subQ0,subQ1])]}),makeQuery(id+"F3.opExtrude","SWEPT_EDGE",EDGE,{"disambiguationData":[OSD([subQ0,subQ1])]})]})});}
            var Q7;
            Q7=makeQuery(id+"F3.opExtrude","SWEPT_EDGE",EDGE,{"disambiguationData":[OSD([sQuery(id+"F1.wireOp",EDGE,"E61.MirrorCS"),sQuery(id+"F1.wireOp",EDGE,"E64.MirrorCS")])]});
            fillet(context, id + "F9", {"entities" : qUnion([Q0, Q1, Q2, Q3, Q4, Q5, Q6, Q7]), "radius" : 5 * mm, "tangentPropagation" : true, "allowEdgeOverflow" : false});
        }
    });
